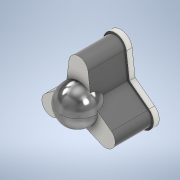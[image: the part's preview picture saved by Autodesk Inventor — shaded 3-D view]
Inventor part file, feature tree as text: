
AUTODESK INVENTOR PART (.ipt)
format: ipt  version: 2022 (Build 260153000, 153)  size: 286,208 bytes
history: native  units: mm
features: other x3, sketch x3, extrude x2, pattern_circular x1, hole x1
ambient origin geometry x8: Origin, YZ Plane, XZ Plane, XY Plane, X Axis, Y Axis, Z Axis, Center Point
bodies: Body1 (feature_tree)
feature tree (10):
  other  "フォーム1"
  other  "作業平面1"
  extrude  "押し出し1"  [1 undecoded]
  extrude  "押し出し2"  Depth=26.0mm
  pattern_circular  "円形状パターン1"  [2 undecoded]
  hole  "穴1"  [1 undecoded]
  sketch  "スケッチ2"
  sketch  "スケッチ3"
  sketch  "スケッチ4"
  other  "ソリッド1"
note: 4 required parameter values undecoded (feature->parameter linkage not recoverable at this tier; creation-order binding heuristic only, values carry confidence <= 0.55)
